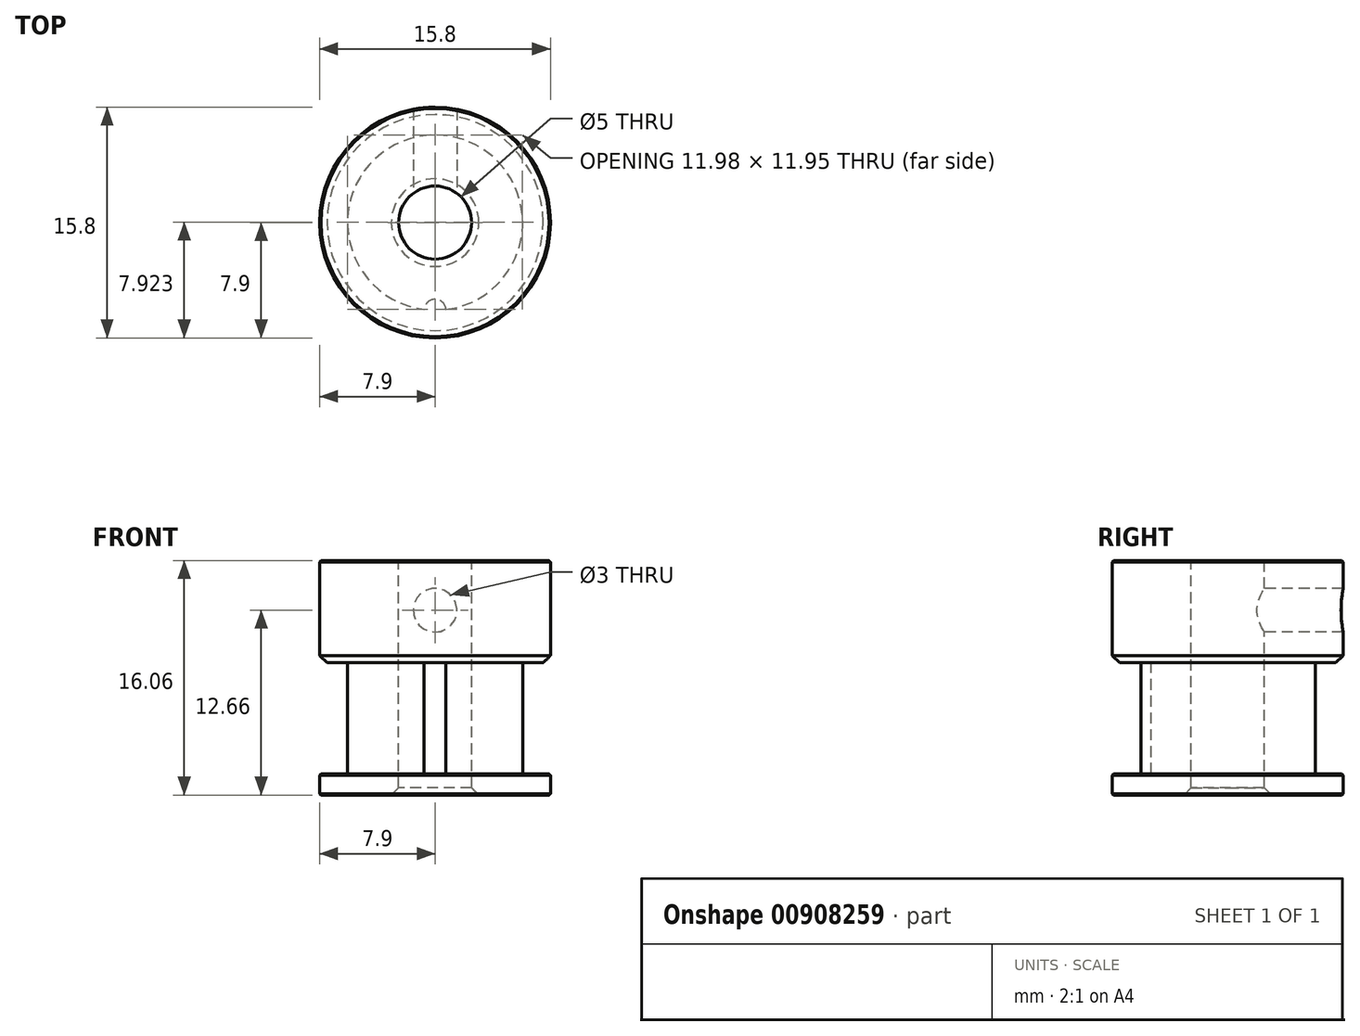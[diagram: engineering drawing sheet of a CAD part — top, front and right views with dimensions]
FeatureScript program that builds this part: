
annotation { "Feature Type Name" : "Feature", "Feature Type Description" : "" }
export const myFeature = defineFeature(function(context is Context, id is Id, definition is map)
    precondition{}
    {
        {
            var Q0;
            Q0=qCreatedBy(makeId("Top.planeOp"),FACE);
            var sketch = newSketch(context, id + "F0", { "sketchPlane" : qUnion([Q0])});
            skCircle(sketch, "E0", {"center": v(0, 0) * mm, "radius": 7.9 * mm});
            skSolve(sketch);
        }
        {
            var Q0;
            Q0 = qSketchRegion(id + "F0", true);
            extrude(context, id + "F1", {"entities" : qUnion([Q0]), "depth" : 1.46 * mm, "offsetDistance" : 25 * mm});
        }
        {
            var Q0;
            Q0=makeQuery(id+"F1.opExtrude","CAP_FACE",FACE,{"disambiguationData":[OSD([sQuery(id+"F0.wireOp",EDGE,"E0")])],"isStart":false});
            var sketch = newSketch(context, id + "F2", { "sketchPlane" : qUnion([Q0])});
            skCircle(sketch, "E1", {"center": v(0, 0) * mm, "radius": 6 * mm});
            skSolve(sketch);
        }
        {
            var Q0;
            Q0 = qSketchRegion(id + "F2", true);
            extrude(context, id + "F3", {"entities" : qUnion([Q0]), "operationType" : NewBodyOperationType.ADD, "depth" : 7.6 * mm, "offsetDistance" : 25 * mm});
        }
        {
            var Q0;
            Q0=makeQuery(id+"F3.opExtrude","CAP_FACE",FACE,{"disambiguationData":[OSD([sQuery(id+"F2.wireOp",EDGE,"E1")])],"isStart":false});
            var sketch = newSketch(context, id + "F4", { "sketchPlane" : qUnion([Q0])});
            skCircle(sketch, "E2", {"center": v(0, -6) * mm, "radius": 0.75 * mm});
            skSolve(sketch);
        }
        {
            var Q0;
            Q0 = qSketchRegion(id + "F4", true);
            extrude(context, id + "F5", {"entities" : qUnion([Q0]), "operationType" : NewBodyOperationType.REMOVE, "oppositeDirection" : true, "depth" : 7.6 * mm, "offsetDistance" : 25 * mm});
        }
        {
            var Q0;
            Q0=makeQuery(id+"F3.opExtrude","CAP_FACE",FACE,{"disambiguationData":[OSD([sQuery(id+"F2.wireOp",EDGE,"E1")])],"isStart":false});
            var sketch = newSketch(context, id + "F6", { "sketchPlane" : qUnion([Q0])});
            skCircle(sketch, "E3", {"center": v(0, 0) * mm, "radius": 7.9 * mm});
            skSolve(sketch);
        }
        {
            var Q0;
            Q0 = qSketchRegion(id + "F6", true);
            extrude(context, id + "F7", {"entities" : qUnion([Q0]), "operationType" : NewBodyOperationType.ADD, "depth" : 7 * mm, "offsetDistance" : 25 * mm});
        }
        {
            var Q0;
            Q0=qCreatedBy(makeId("Front.planeOp"),FACE);
            var sketch = newSketch(context, id + "F8", { "sketchPlane" : qUnion([Q0])});
            skCircle(sketch, "E4", {"center": v(0, 12.66) * mm, "radius": 1.5 * mm});
            skSolve(sketch);
        }
        {
            var Q0;
            Q0 = qSketchRegion(id + "F8", true);
            extrude(context, id + "F9", {"entities" : qUnion([Q0]), "operationType" : NewBodyOperationType.REMOVE, "oppositeDirection" : true, "depth" : 25 * mm, "offsetDistance" : 25 * mm});
        }
        {
            var Q0;
            Q0=makeQuery(id+"F7.opExtrude","CAP_FACE",FACE,{"disambiguationData":[OSD([sQuery(id+"F6.wireOp",EDGE,"E3")])],"isStart":false});
            var sketch = newSketch(context, id + "F10", { "sketchPlane" : qUnion([Q0])});
            skCircle(sketch, "E5", {"center": v(0, 0) * mm, "radius": 2.5 * mm});
            skSolve(sketch);
        }
        {
            var Q0;
            Q0 = qSketchRegion(id + "F10", true);
            extrude(context, id + "F11", {"entities" : qUnion([Q0]), "operationType" : NewBodyOperationType.REMOVE, "oppositeDirection" : true, "depth" : 25 * mm, "offsetDistance" : 25 * mm});
        }
        {
            var Q0;
            Q0=makeQuery(id+"F7.opExtrude","CAP_EDGE",EDGE,{"disambiguationData":[OSD([sQuery(id+"F6.wireOp",EDGE,"E3")])],"isStart":true});
            var Q1;
            Q1=makeQuery(id+"F11.boolean.opBoolean","INTERSECT",EDGE,{"derivedFrom":[makeQuery(id+"F1.opExtrude","CAP_FACE",FACE,{"disambiguationData":[OSD([sQuery(id+"F0.wireOp",EDGE,"E0")])],"isStart":true}),makeQuery(id+"F11.opExtrude","SWEPT_FACE",FACE,{"disambiguationData":[OSD([sQuery(id+"F10.wireOp",EDGE,"E5")])]})]});
            var Q2;
            Q2=makeQuery(id+"F11.boolean.opBoolean","COPY",EDGE,{"derivedFrom":makeQuery(id+"F11.opExtrude","CAP_EDGE",EDGE,{"disambiguationData":[OSD([sQuery(id+"F10.wireOp",EDGE,"E5")])],"isStart":true})});
            chamfer(context, id + "F12", {"entities" : qUnion([Q0, Q1, Q2]), "width" : 0.5 * mm, "tangentPropagation" : true});
        }
        {
            var Q0;
            Q0=makeQuery(id+"F1.opExtrude","CAP_EDGE",EDGE,{"disambiguationData":[OSD([sQuery(id+"F0.wireOp",EDGE,"E0")])],"isStart":true});
            var Q1;
            Q1=makeQuery(id+"F1.opExtrude","CAP_EDGE",EDGE,{"disambiguationData":[OSD([sQuery(id+"F0.wireOp",EDGE,"E0")])],"isStart":false});
            var Q2;
            Q2=makeQuery(id+"F7.opExtrude","CAP_EDGE",EDGE,{"disambiguationData":[OSD([sQuery(id+"F6.wireOp",EDGE,"E3")])],"isStart":false});
            chamfer(context, id + "F13", {"entities" : qUnion([Q0, Q1, Q2]), "width" : 0.1 * mm, "tangentPropagation" : true});
        }
    });
